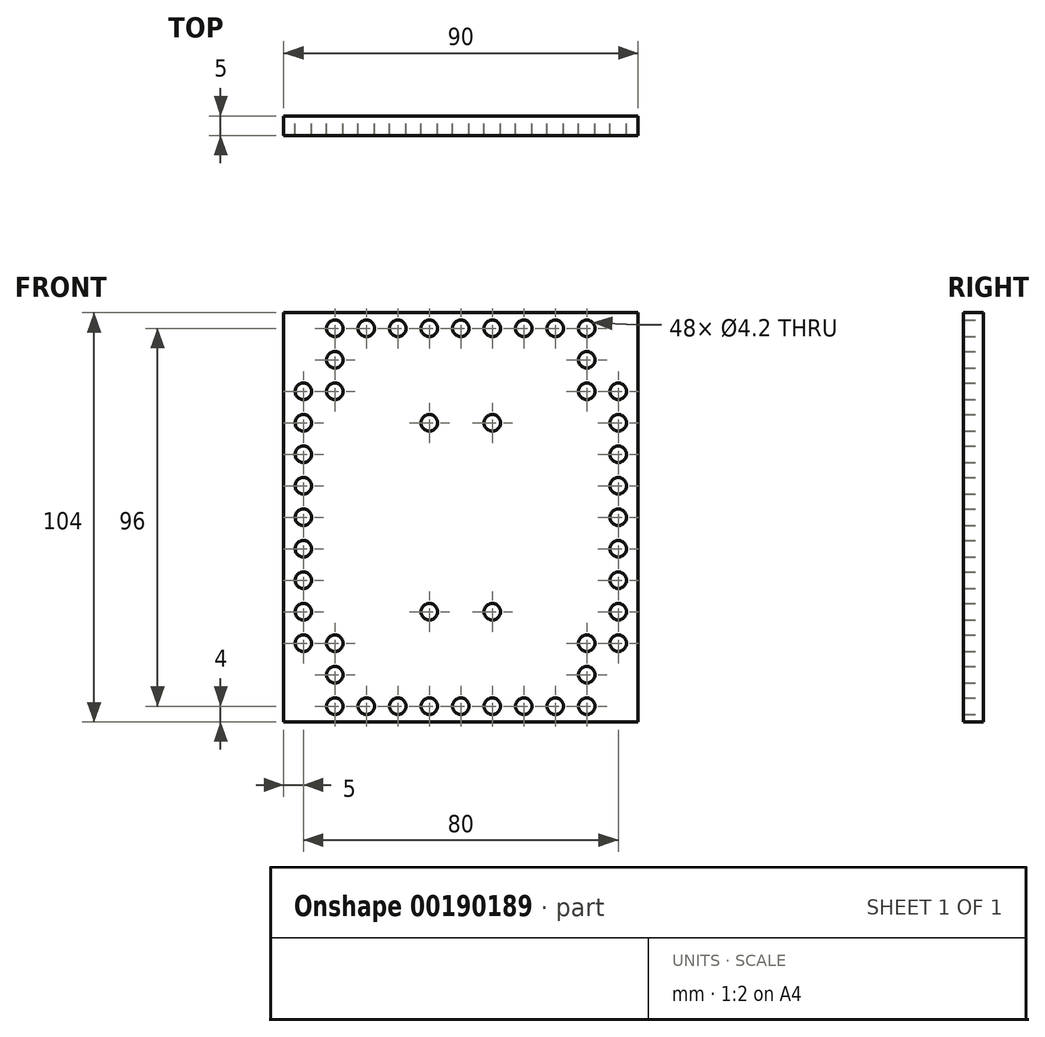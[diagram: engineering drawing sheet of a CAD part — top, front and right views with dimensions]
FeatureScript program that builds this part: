
annotation { "Feature Type Name" : "Feature", "Feature Type Description" : "" }
export const myFeature = defineFeature(function(context is Context, id is Id, definition is map)
    precondition{}
    {
        {
            var Q0;
            Q0=qCreatedBy(makeId("Front.planeOp"),FACE);
            var sketch = newSketch(context, id + "F0", { "sketchPlane" : qUnion([Q0])});
            skLineSegment(sketch, "E0.bottom", {"start": v(-45, 52) * mm, "end": v(45, 52) * mm});
            skLineSegment(sketch, "E0.top", {"start": v(-45, -52) * mm, "end": v(45, -52) * mm});
            skLineSegment(sketch, "E0.left", {"start": v(-45, 52) * mm, "end": v(-45, -52) * mm});
            skLineSegment(sketch, "E0.right", {"start": v(45, 52) * mm, "end": v(45, -52) * mm});
            skPoint(sketch, "E0.middle", {"position": v(0, 0) * mm});
            skLineSegment(sketch, "E1", {"start": v(-40, 52) * mm, "end": v(-40, -52) * mm, "construction": true});
            skLineSegment(sketch, "E2", {"start": v(-45, -48) * mm, "end": v(45, -48) * mm, "construction": true});
            skLineSegment(sketch, "E3", {"start": v(-32, -52) * mm, "end": v(-32, 52) * mm, "construction": true});
            skLineSegment(sketch, "E4", {"start": v(-45, -32) * mm, "end": v(45, -32) * mm, "construction": true});
            skCircle(sketch, "E5", {"center": v(-32, -48) * mm, "radius": 2.1 * mm});
            skCircle(sketch, "E6.0.1.0", {"center": v(-32, 48) * mm, "radius": 2.1 * mm});
            skCircle(sketch, "E6.1.0.0", {"center": v(-24, -48) * mm, "radius": 2.1 * mm});
            skCircle(sketch, "E6.1.1.0", {"center": v(-24, 48) * mm, "radius": 2.1 * mm});
            skCircle(sketch, "E6.2.0.0", {"center": v(-16, -48) * mm, "radius": 2.1 * mm});
            skCircle(sketch, "E6.2.1.0", {"center": v(-16, 48) * mm, "radius": 2.1 * mm});
            skCircle(sketch, "E6.3.0.0", {"center": v(-8, -48) * mm, "radius": 2.1 * mm});
            skCircle(sketch, "E6.3.1.0", {"center": v(-8, 48) * mm, "radius": 2.1 * mm});
            skCircle(sketch, "E6.4.0.0", {"center": v(0, -48) * mm, "radius": 2.1 * mm});
            skCircle(sketch, "E6.4.1.0", {"center": v(0, 48) * mm, "radius": 2.1 * mm});
            skCircle(sketch, "E6.5.0.0", {"center": v(8, -48) * mm, "radius": 2.1 * mm});
            skCircle(sketch, "E6.5.1.0", {"center": v(8, 48) * mm, "radius": 2.1 * mm});
            skCircle(sketch, "E6.6.0.0", {"center": v(16, -48) * mm, "radius": 2.1 * mm});
            skCircle(sketch, "E6.6.1.0", {"center": v(16, 48) * mm, "radius": 2.1 * mm});
            skCircle(sketch, "E6.7.0.0", {"center": v(24, -48) * mm, "radius": 2.1 * mm});
            skCircle(sketch, "E6.7.1.0", {"center": v(24, 48) * mm, "radius": 2.1 * mm});
            skCircle(sketch, "E6.8.0.0", {"center": v(32, -48) * mm, "radius": 2.1 * mm});
            skCircle(sketch, "E6.8.1.0", {"center": v(32, 48) * mm, "radius": 2.1 * mm});
            skLineSegment(sketch, "E6.direction1", {"start": v(-32, -48) * mm, "end": v(-24, -48) * mm, "construction": true});
            skLineSegment(sketch, "E6.direction2", {"start": v(-32, -48) * mm, "end": v(-32, 48) * mm, "construction": true});
            skCircle(sketch, "E7", {"center": v(-40, -32) * mm, "radius": 2.1 * mm});
            skCircle(sketch, "E8.0.1.0", {"center": v(-40, -24) * mm, "radius": 2.1 * mm});
            skCircle(sketch, "E8.0.2.0", {"center": v(-40, -16) * mm, "radius": 2.1 * mm});
            skCircle(sketch, "E8.0.3.0", {"center": v(-40, -8) * mm, "radius": 2.1 * mm});
            skCircle(sketch, "E8.0.4.0", {"center": v(-40, 0) * mm, "radius": 2.1 * mm});
            skCircle(sketch, "E8.0.5.0", {"center": v(-40, 8) * mm, "radius": 2.1 * mm});
            skCircle(sketch, "E8.0.6.0", {"center": v(-40, 16) * mm, "radius": 2.1 * mm});
            skCircle(sketch, "E8.0.7.0", {"center": v(-40, 24) * mm, "radius": 2.1 * mm});
            skCircle(sketch, "E8.0.8.0", {"center": v(-40, 32) * mm, "radius": 2.1 * mm});
            skCircle(sketch, "E8.1.0.0", {"center": v(40, -32) * mm, "radius": 2.1 * mm});
            skCircle(sketch, "E8.1.1.0", {"center": v(40, -24) * mm, "radius": 2.1 * mm});
            skCircle(sketch, "E8.1.2.0", {"center": v(40, -16) * mm, "radius": 2.1 * mm});
            skCircle(sketch, "E8.1.3.0", {"center": v(40, -8) * mm, "radius": 2.1 * mm});
            skCircle(sketch, "E8.1.4.0", {"center": v(40, 0) * mm, "radius": 2.1 * mm});
            skCircle(sketch, "E8.1.5.0", {"center": v(40, 8) * mm, "radius": 2.1 * mm});
            skCircle(sketch, "E8.1.6.0", {"center": v(40, 16) * mm, "radius": 2.1 * mm});
            skCircle(sketch, "E8.1.7.0", {"center": v(40, 24) * mm, "radius": 2.1 * mm});
            skCircle(sketch, "E8.1.8.0", {"center": v(40, 32) * mm, "radius": 2.1 * mm});
            skLineSegment(sketch, "E8.direction1", {"start": v(-40, -32) * mm, "end": v(40, -32) * mm, "construction": true});
            skLineSegment(sketch, "E8.direction2", {"start": v(-40, -32) * mm, "end": v(-40, -24) * mm, "construction": true});
            skCircle(sketch, "E9", {"center": v(-32, -32) * mm, "radius": 2.1 * mm});
            skPoint(sketch, "E10", {"position": v(-32, -40) * mm});
            skCircle(sketch, "E11", {"center": v(-32, -40) * mm, "radius": 2.1 * mm});
            skCircle(sketch, "E12.MirrorC", {"center": v(32, -32) * mm, "radius": 2.1 * mm});
            skCircle(sketch, "E13.MirrorC", {"center": v(32, -40) * mm, "radius": 2.1 * mm});
            skCircle(sketch, "E14.MirrorC", {"center": v(-32, 32) * mm, "radius": 2.1 * mm});
            skPoint(sketch, "E15.MirrorP", {"position": v(-32, 40) * mm});
            skCircle(sketch, "E16.MirrorC", {"center": v(32, 32) * mm, "radius": 2.1 * mm});
            skCircle(sketch, "E17.MirrorC", {"center": v(32, 40) * mm, "radius": 2.1 * mm});
            skCircle(sketch, "E18.MirrorC", {"center": v(-32, 40) * mm, "radius": 2.1 * mm});
            skPoint(sketch, "E19", {"position": v(-8, 24) * mm});
            skCircle(sketch, "E20", {"center": v(-8, 24) * mm, "radius": 2.1 * mm});
            skCircle(sketch, "E21.MirrorC", {"center": v(8, 24) * mm, "radius": 2.1 * mm});
            skCircle(sketch, "E22.MirrorC", {"center": v(-8, -24) * mm, "radius": 2.1 * mm});
            skCircle(sketch, "E23.MirrorC", {"center": v(8, -24) * mm, "radius": 2.1 * mm});
            skSolve(sketch);
        }
        {
            var Q0;
            Q0=makeQuery(id+"F0.imprint","IMPRINT",FACE,{"disambiguationData":[TD([[makeQuery(id+"F0.imprint","IMPRINT",EDGE,{"derivedFrom":sQuery(id+"F0.wireOp",EDGE,"E0.bottom")}),-1.0]])]});
            extrude(context, id + "F1", {"entities" : qUnion([Q0]), "depth" : 5 * mm});
        }
    });
